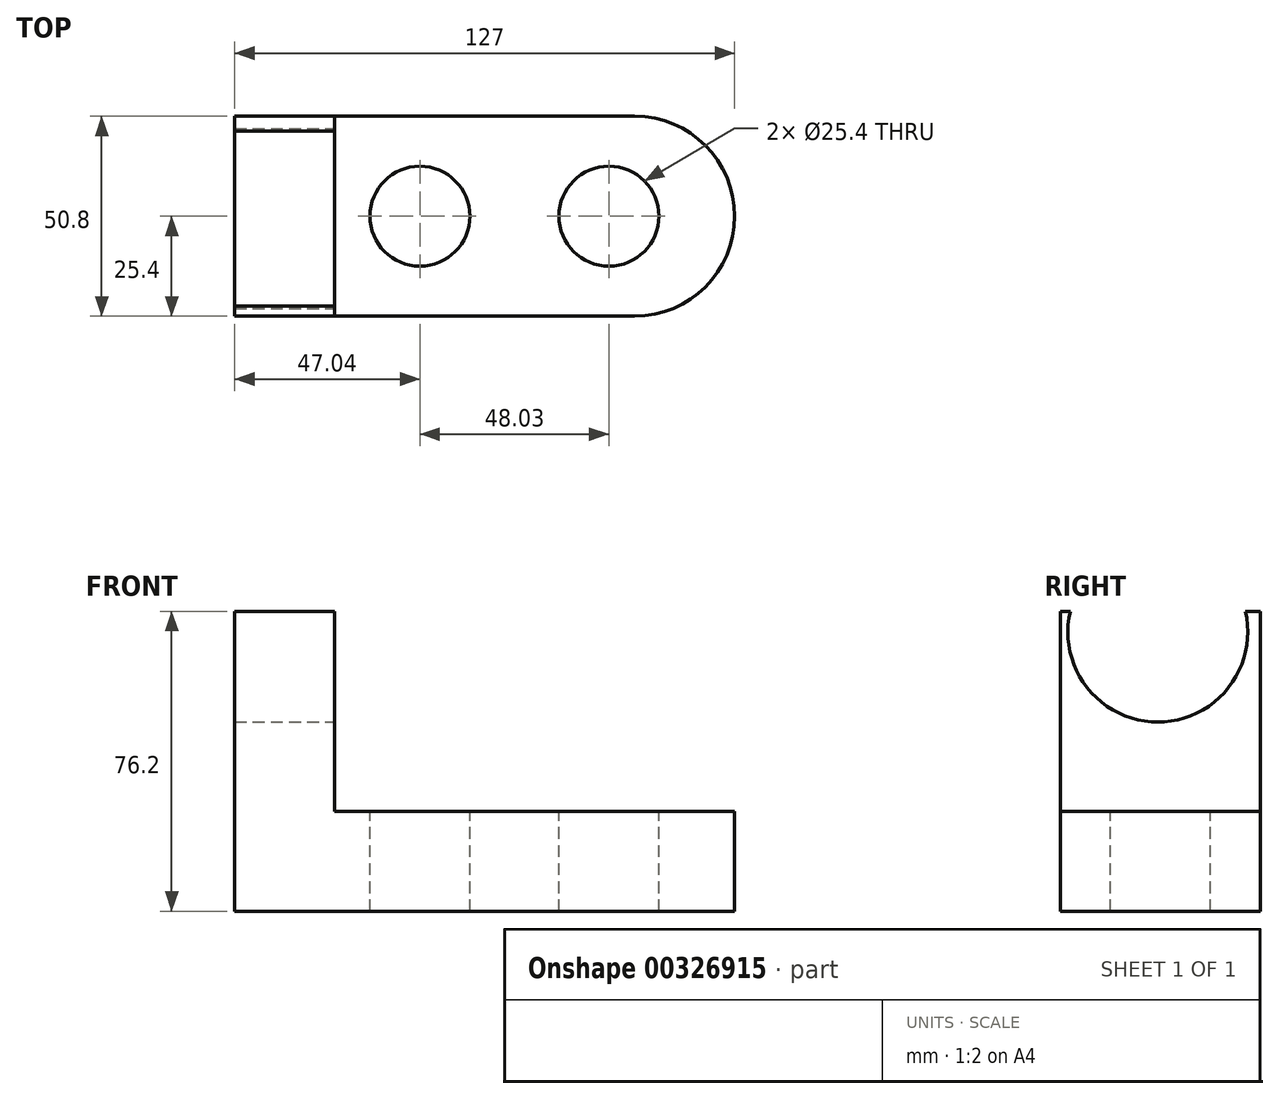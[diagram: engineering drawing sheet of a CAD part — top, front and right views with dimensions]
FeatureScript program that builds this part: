
annotation { "Feature Type Name" : "Feature", "Feature Type Description" : "" }
export const myFeature = defineFeature(function(context is Context, id is Id, definition is map)
    precondition{}
    {
        {
            var Q0;
            Q0=qCreatedBy(makeId("Front.planeOp"),FACE);
            var sketch = newSketch(context, id + "F0", { "sketchPlane" : qUnion([Q0])});
            skLineSegment(sketch, "E0", {"start": v(-47.04, -50.6) * mm, "end": v(54.56, -50.6) * mm});
            skLineSegment(sketch, "E1", {"start": v(-47.04, -50.6) * mm, "end": v(-47.04, 25.6) * mm});
            skLineSegment(sketch, "E2", {"start": v(-47.04, 25.6) * mm, "end": v(54.56, 25.6) * mm});
            skLineSegment(sketch, "E3", {"start": v(54.56, 25.6) * mm, "end": v(54.56, -50.6) * mm});
            skSolve(sketch);
        }
        {
            var Q0;
            Q0=makeQuery(id+"F0.imprint","IMPRINT",FACE,{"disambiguationData":[TD([[makeQuery(id+"F0.imprint","IMPRINT",EDGE,{"derivedFrom":sQuery(id+"F0.wireOp",EDGE,"E0")}),1.0]])]});
            extrude(context, id + "F1", {"entities" : qUnion([Q0]), "depth" : 50.8 * mm});
        }
        {
            var Q0;
            Q0=makeQuery(id+"F1.opExtrude","SWEPT_FACE",FACE,{"disambiguationData":[OSD([sQuery(id+"F0.wireOp",EDGE,"E2")])]});
            var sketch = newSketch(context, id + "F2", { "sketchPlane" : qUnion([Q0])});
            skLineSegment(sketch, "E4", {"start": v(-47.04, -50.8) * mm, "end": v(-21.64, -50.8) * mm});
            skLineSegment(sketch, "E5", {"start": v(-47.04, -50.8) * mm, "end": v(-47.04, 0) * mm});
            skLineSegment(sketch, "E6", {"start": v(-47.04, 0) * mm, "end": v(-21.64, 0) * mm});
            skLineSegment(sketch, "E7", {"start": v(-21.64, 0) * mm, "end": v(-21.64, -53.2) * mm});
            skSolve(sketch);
        }
        {
            var Q0;
            {var subQ1=sQuery(id+"F0.wireOp",EDGE,"E2");var subQ6=makeQuery(id+"F1.opExtrude","SWEPT_EDGE",EDGE,{"disambiguationData":[OSD([subQ1,sQuery(id+"F0.wireOp",EDGE,"E3")])]});Q0=makeQuery(id+"F2.imprint","IMPRINT",FACE,{"disambiguationData":[TD([[makeQuery(id+"F2.imprint","IMPRINT",EDGE,{"derivedFrom":subQ6}),1.0]])]});}
            extrude(context, id + "F3", {"entities" : qUnion([Q0]), "operationType" : NewBodyOperationType.REMOVE, "oppositeDirection" : true, "depth" : 50.8 * mm});
        }
        {
            var Q0;
            Q0=makeQuery(id+"F1.opExtrude","SWEPT_FACE",FACE,{"disambiguationData":[OSD([sQuery(id+"F0.wireOp",EDGE,"E3")])]});
            var sketch = newSketch(context, id + "F4", { "sketchPlane" : qUnion([Q0])});
            skLineSegment(sketch, "E8", {"start": v(-25.4, -25.2) * mm, "end": v(-25.4, -50.6) * mm});
            skSolve(sketch);
        }
        {
            var Q0;
            {var subQ0=sQuery(id+"F4.wireOp",EDGE,"E8");Q0=makeQuery(id+"F4.imprint","IMPRINT",FACE,{"disambiguationData":[TD([[makeQuery(id+"F4.imprint","IMPRINT",EDGE,{"derivedFrom":subQ0}),1.0]])]});}
            var Q1;
            Q1=sQuery(id+"F4.wireOp",EDGE,"E8");
            revolve(context, id + "F5", {"operationType" : NewBodyOperationType.ADD, "entities" : qUnion([Q0]), "axis" : qUnion([Q1]), "revolveType" : RevolveType.FULL});
        }
        {
            var Q0;
            {var subQ0=sQuery(id+"F0.wireOp",EDGE,"E3");var subQ1=sQuery(id+"F0.wireOp",EDGE,"E2");Q0=makeQuery(id+"F5.boolean.opBoolean","MERGE",FACE,{"derivedFrom":[makeQuery(id+"F3.boolean.opBoolean","COPY",FACE,{"derivedFrom":makeQuery(id+"F3.opExtrude","CAP_FACE",FACE,{"disambiguationData":[OSD([subQ1,subQ0,sQuery(id+"F2.wireOp",EDGE,"E7")])],"isStart":false})}),makeQuery(id+"F5.opRevolve","SWEPT_FACE",FACE,{"disambiguationData":[OSD([subQ1,subQ0])]})]});}
            var sketch = newSketch(context, id + "F6", { "sketchPlane" : qUnion([Q0])});
            skCircle(sketch, "E9", {"center": v(48.03, -25.4) * mm, "radius": 12.7 * mm});
            skPoint(sketch, "E9.centerSnap0", {"position": v(79.96, -25.4) * mm});
            skCircle(sketch, "E10", {"center": v(0, -25.4) * mm, "radius": 12.7 * mm});
            skSolve(sketch);
        }
        {
            var Q0;
            Q0=makeQuery(id+"F6.imprint","IMPRINT",FACE,{"disambiguationData":[TD([[makeQuery(id+"F6.imprint","IMPRINT",EDGE,{"derivedFrom":sQuery(id+"F6.wireOp",EDGE,"E10")}),1.0]])]});
            var Q1;
            Q1=makeQuery(id+"F6.imprint","IMPRINT",FACE,{"disambiguationData":[TD([[makeQuery(id+"F6.imprint","IMPRINT",EDGE,{"derivedFrom":sQuery(id+"F6.wireOp",EDGE,"E9")}),1.0]])]});
            extrude(context, id + "F7", {"entities" : qUnion([Q0, Q1]), "operationType" : NewBodyOperationType.REMOVE, "oppositeDirection" : true, "depth" : 101.6 * mm});
        }
        {
            var Q0;
            Q0=makeQuery(id+"F3.boolean.opBoolean","COPY",FACE,{"derivedFrom":makeQuery(id+"F3.opExtrude","SWEPT_FACE",FACE,{"disambiguationData":[OSD([sQuery(id+"F2.wireOp",EDGE,"E7")])]})});
            var sketch = newSketch(context, id + "F8", { "sketchPlane" : qUnion([Q0])});
            skArc(sketch, "E11", {"start": v(-48.25, 25.6) * mm, "mid": v(-26, -2.49) * mm, "end": v(-3.75, 25.6) * mm});
            skSolve(sketch);
        }
        {
            var Q0;
            {var subQ0=sQuery(id+"F8.wireOp",EDGE,"E11");Q0=makeQuery(id+"F8.imprint","IMPRINT",FACE,{"disambiguationData":[TD([[makeQuery(id+"F8.imprint","IMPRINT",EDGE,{"derivedFrom":subQ0}),1.0]])]});}
            extrude(context, id + "F9", {"entities" : qUnion([Q0]), "operationType" : NewBodyOperationType.REMOVE, "oppositeDirection" : true, "depth" : 101.6 * mm});
        }
    });
